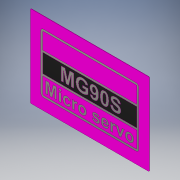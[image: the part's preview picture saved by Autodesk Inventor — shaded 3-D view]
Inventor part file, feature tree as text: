
AUTODESK INVENTOR PART (.ipt)
format: ipt  version: 2019 (Build 230136000, 136)  size: 483,328 bytes
history: native  units: mm
features: extrude x2, sketch x2, fillet x1
ambient origin geometry x8: Origin, YZ Plane, XZ Plane, XY Plane, X Axis, Y Axis, Z Axis, Center Point
bodies: Solid1 (feature_tree)
feature tree (5):
  extrude  "Extrusion1"  Depth=10.0mm
  fillet  "Fillet1"  Radius=0.05mm
  extrude  "Extrusion3"  Depth=12.0mm
  sketch  "Sketch1"  dims[d0=14.5mm d1=10.0mm d2=0.05mm d3=0.0mm]
  sketch  "Sketch3"  dims[d50=0.1mm d51=12.0mm d52=7.25mm d53=0.35mm d54=0.25mm d55=0.25mm d56=0.25mm d57=2.25mm d64=0.25mm d65=0.25mm d66=0.0001mm d67=0.0mm]
